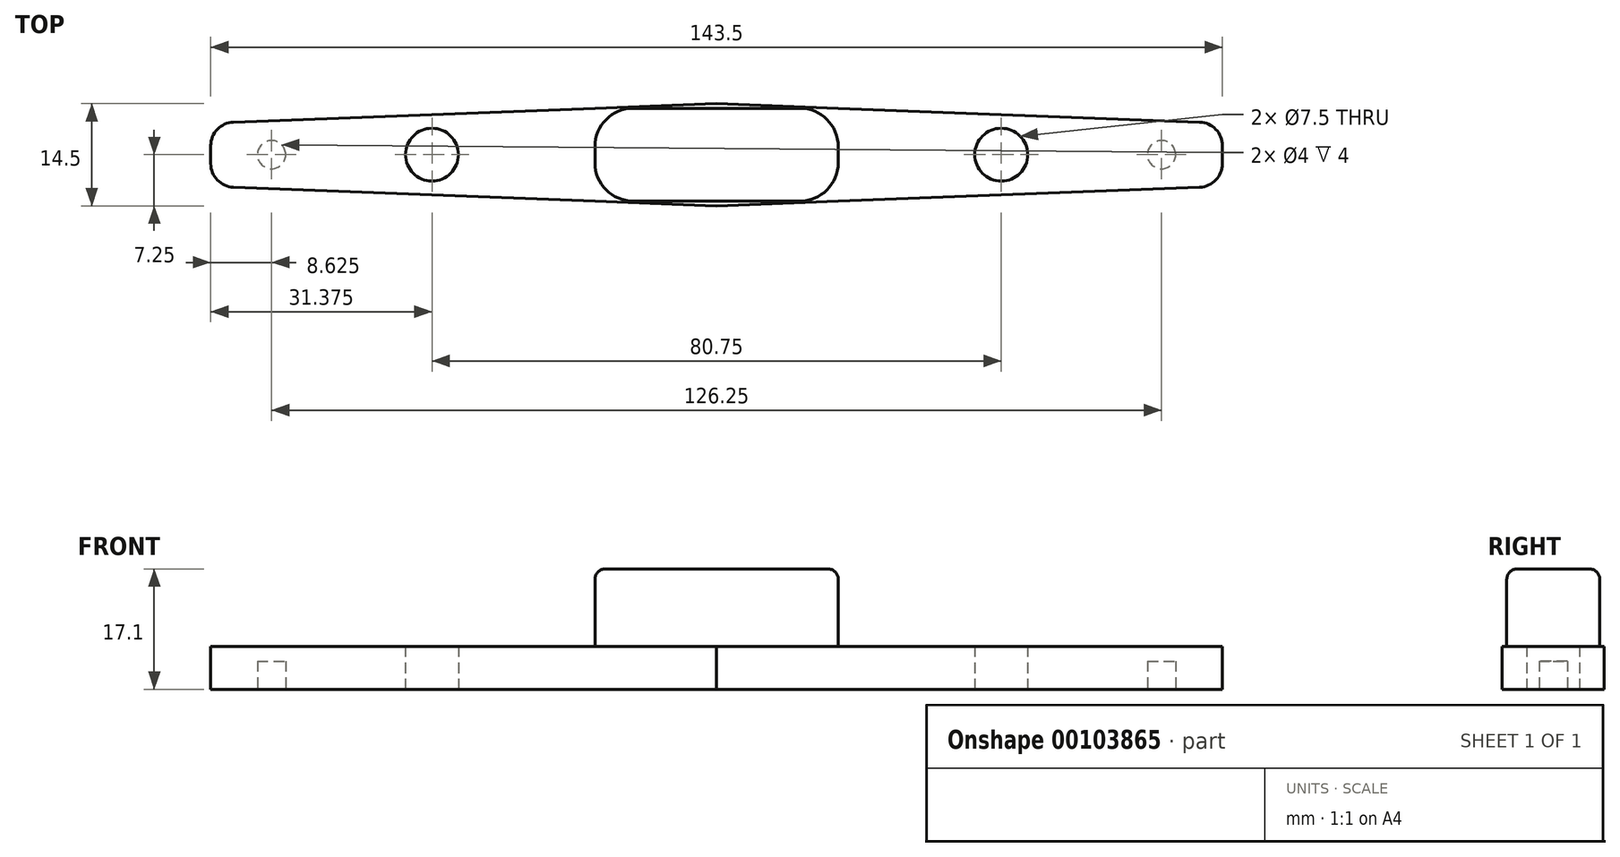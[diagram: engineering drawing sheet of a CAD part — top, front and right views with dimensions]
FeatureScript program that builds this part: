
annotation { "Feature Type Name" : "Feature", "Feature Type Description" : "" }
export const myFeature = defineFeature(function(context is Context, id is Id, definition is map)
    precondition{}
    {
        {
            var Q0;
            Q0=qCreatedBy(makeId("Top.planeOp"),FACE);
            var sketch = newSketch(context, id + "F0", { "sketchPlane" : qUnion([Q0])});
            skLineSegment(sketch, "E0", {"start": v(0, 7.25) * mm, "end": v(-71.75, 4.5) * mm});
            skLineSegment(sketch, "E1", {"start": v(-71.75, 4.5) * mm, "end": v(-71.75, -4.5) * mm});
            skLineSegment(sketch, "E2", {"start": v(-71.75, -4.5) * mm, "end": v(0, -7.25) * mm});
            skLineSegment(sketch, "E3", {"start": v(0, -7.25) * mm, "end": v(71.75, -4.5) * mm});
            skLineSegment(sketch, "E4", {"start": v(71.75, -4.5) * mm, "end": v(71.75, 4.5) * mm});
            skLineSegment(sketch, "E5", {"start": v(71.75, 4.5) * mm, "end": v(0, 7.25) * mm});
            skCircle(sketch, "E6", {"center": v(-40.37, 0) * mm, "radius": 3.75 * mm});
            skCircle(sketch, "E7", {"center": v(40.38, 0) * mm, "radius": 3.75 * mm});
            skSolve(sketch);
        }
        {
            var Q0;
            Q0=makeQuery(id+"F0.imprint","IMPRINT",FACE,{"disambiguationData":[TD([[makeQuery(id+"F0.imprint","IMPRINT",EDGE,{"derivedFrom":sQuery(id+"F0.wireOp",EDGE,"E0")}),1.0]])]});
            extrude(context, id + "F1", {"entities" : qUnion([Q0]), "depth" : 6.1 * mm});
        }
        {
            var Q0;
            Q0=makeQuery(id+"F1.opExtrude","CAP_FACE",FACE,{"disambiguationData":[OSD([sQuery(id+"F0.wireOp",EDGE,"E0"),sQuery(id+"F0.wireOp",EDGE,"E1"),sQuery(id+"F0.wireOp",EDGE,"E2"),sQuery(id+"F0.wireOp",EDGE,"E3"),sQuery(id+"F0.wireOp",EDGE,"E4"),sQuery(id+"F0.wireOp",EDGE,"E5"),sQuery(id+"F0.wireOp",EDGE,"E6"),sQuery(id+"F0.wireOp",EDGE,"E7")])],"isStart":false});
            var sketch = newSketch(context, id + "F2", { "sketchPlane" : qUnion([Q0])});
            skLineSegment(sketch, "E8.bottom", {"start": v(17.25, -6.59) * mm, "end": v(-17.25, -6.59) * mm});
            skLineSegment(sketch, "E8.top", {"start": v(17.25, 6.59) * mm, "end": v(-17.25, 6.59) * mm});
            skLineSegment(sketch, "E8.left", {"start": v(17.25, -6.59) * mm, "end": v(17.25, 6.59) * mm});
            skLineSegment(sketch, "E8.right", {"start": v(-17.25, -6.59) * mm, "end": v(-17.25, 6.59) * mm});
            skPoint(sketch, "E8.middle", {"position": v(0, 0) * mm});
            skSolve(sketch);
        }
        {
            var Q0;
            Q0 = qSketchRegion(id + "F2", true);
            extrude(context, id + "F3", {"entities" : qUnion([Q0]), "operationType" : NewBodyOperationType.ADD, "depth" : 11 * mm});
        }
        {
            var Q0;
            Q0=makeQuery(id+"F3.opExtrude","SWEPT_EDGE",EDGE,{"disambiguationData":[OSD([sQuery(id+"F0.wireOp",EDGE,"E2"),sQuery(id+"F2.wireOp",EDGE,"E8.bottom"),sQuery(id+"F2.wireOp",EDGE,"E8.right")])]});
            var Q1;
            Q1=makeQuery(id+"F3.opExtrude","SWEPT_EDGE",EDGE,{"disambiguationData":[OSD([sQuery(id+"F0.wireOp",EDGE,"E0"),sQuery(id+"F2.wireOp",EDGE,"E8.top"),sQuery(id+"F2.wireOp",EDGE,"E8.right")])]});
            var Q2;
            Q2=makeQuery(id+"F3.opExtrude","SWEPT_EDGE",EDGE,{"disambiguationData":[OSD([sQuery(id+"F0.wireOp",EDGE,"E3"),sQuery(id+"F2.wireOp",EDGE,"E8.bottom"),sQuery(id+"F2.wireOp",EDGE,"E8.left")])]});
            var Q3;
            Q3=makeQuery(id+"F3.opExtrude","SWEPT_EDGE",EDGE,{"disambiguationData":[OSD([sQuery(id+"F0.wireOp",EDGE,"E5"),sQuery(id+"F2.wireOp",EDGE,"E8.top"),sQuery(id+"F2.wireOp",EDGE,"E8.left")])]});
            fillet(context, id + "F4", {"entities" : qUnion([Q0, Q1, Q2, Q3]), "radius" : 5.44 * mm, "tangentPropagation" : true, "allowEdgeOverflow" : false});
        }
        {
            var Q0;
            Q0=makeQuery(id+"F3.opExtrude","CAP_EDGE",EDGE,{"disambiguationData":[OSD([sQuery(id+"F2.wireOp",EDGE,"E8.top")])],"isStart":false});
            var Q1;
            {var subQ0=sQuery(id+"F2.wireOp",EDGE,"E8.left");var subQ1=sQuery(id+"F2.wireOp",EDGE,"E8.top");Q1=makeQuery(id+"F4.opFillet","BLEND_EDGE",EDGE,{"blendedFrom":[makeQuery(id+"F3.opExtrude","SWEPT_EDGE",EDGE,{"disambiguationData":[OSD([sQuery(id+"F0.wireOp",EDGE,"E5"),subQ1,subQ0])]}),makeQuery(id+"F3.opExtrude","CAP_FACE",FACE,{"disambiguationData":[OSD([sQuery(id+"F2.wireOp",EDGE,"E8.bottom"),subQ1,subQ0,sQuery(id+"F2.wireOp",EDGE,"E8.right")])],"isStart":false})],"blendedInto":[makeQuery(id+"F3.opExtrude","CAP_FACE",FACE,{"disambiguationData":[OSD([sQuery(id+"F2.wireOp",EDGE,"E8.bottom"),subQ1,subQ0,sQuery(id+"F2.wireOp",EDGE,"E8.right")])],"isStart":false})]});}
            var Q2;
            Q2=makeQuery(id+"F3.opExtrude","CAP_EDGE",EDGE,{"disambiguationData":[OSD([sQuery(id+"F2.wireOp",EDGE,"E8.left")])],"isStart":false});
            var Q3;
            {var subQ0=sQuery(id+"F2.wireOp",EDGE,"E8.left");var subQ1=sQuery(id+"F2.wireOp",EDGE,"E8.bottom");Q3=makeQuery(id+"F4.opFillet","BLEND_EDGE",EDGE,{"blendedFrom":[makeQuery(id+"F3.opExtrude","SWEPT_EDGE",EDGE,{"disambiguationData":[OSD([sQuery(id+"F0.wireOp",EDGE,"E3"),subQ1,subQ0])]}),makeQuery(id+"F3.opExtrude","CAP_FACE",FACE,{"disambiguationData":[OSD([subQ1,sQuery(id+"F2.wireOp",EDGE,"E8.top"),subQ0,sQuery(id+"F2.wireOp",EDGE,"E8.right")])],"isStart":false})],"blendedInto":[makeQuery(id+"F3.opExtrude","CAP_FACE",FACE,{"disambiguationData":[OSD([subQ1,sQuery(id+"F2.wireOp",EDGE,"E8.top"),subQ0,sQuery(id+"F2.wireOp",EDGE,"E8.right")])],"isStart":false})]});}
            var Q4;
            Q4=makeQuery(id+"F3.opExtrude","CAP_EDGE",EDGE,{"disambiguationData":[OSD([sQuery(id+"F2.wireOp",EDGE,"E8.bottom")])],"isStart":false});
            var Q5;
            {var subQ0=sQuery(id+"F2.wireOp",EDGE,"E8.right");var subQ1=sQuery(id+"F2.wireOp",EDGE,"E8.bottom");Q5=makeQuery(id+"F4.opFillet","BLEND_EDGE",EDGE,{"blendedFrom":[makeQuery(id+"F3.opExtrude","SWEPT_EDGE",EDGE,{"disambiguationData":[OSD([sQuery(id+"F0.wireOp",EDGE,"E2"),subQ1,subQ0])]}),makeQuery(id+"F3.opExtrude","CAP_FACE",FACE,{"disambiguationData":[OSD([subQ1,sQuery(id+"F2.wireOp",EDGE,"E8.top"),sQuery(id+"F2.wireOp",EDGE,"E8.left"),subQ0])],"isStart":false})],"blendedInto":[makeQuery(id+"F3.opExtrude","CAP_FACE",FACE,{"disambiguationData":[OSD([subQ1,sQuery(id+"F2.wireOp",EDGE,"E8.top"),sQuery(id+"F2.wireOp",EDGE,"E8.left"),subQ0])],"isStart":false})]});}
            var Q6;
            Q6=makeQuery(id+"F3.opExtrude","CAP_EDGE",EDGE,{"disambiguationData":[OSD([sQuery(id+"F2.wireOp",EDGE,"E8.right")])],"isStart":false});
            var Q7;
            {var subQ0=sQuery(id+"F2.wireOp",EDGE,"E8.right");var subQ1=sQuery(id+"F2.wireOp",EDGE,"E8.top");Q7=makeQuery(id+"F4.opFillet","BLEND_EDGE",EDGE,{"blendedFrom":[makeQuery(id+"F3.opExtrude","SWEPT_EDGE",EDGE,{"disambiguationData":[OSD([sQuery(id+"F0.wireOp",EDGE,"E0"),subQ1,subQ0])]}),makeQuery(id+"F3.opExtrude","CAP_FACE",FACE,{"disambiguationData":[OSD([sQuery(id+"F2.wireOp",EDGE,"E8.bottom"),subQ1,sQuery(id+"F2.wireOp",EDGE,"E8.left"),subQ0])],"isStart":false})],"blendedInto":[makeQuery(id+"F3.opExtrude","CAP_FACE",FACE,{"disambiguationData":[OSD([sQuery(id+"F2.wireOp",EDGE,"E8.bottom"),subQ1,sQuery(id+"F2.wireOp",EDGE,"E8.left"),subQ0])],"isStart":false})]});}
            fillet(context, id + "F5", {"entities" : qUnion([Q0, Q1, Q2, Q3, Q4, Q5, Q6, Q7]), "radius" : 1.5 * mm, "tangentPropagation" : true, "allowEdgeOverflow" : false});
        }
        {
            var Q0;
            Q0=makeQuery(id+"F1.opExtrude","CAP_FACE",FACE,{"disambiguationData":[OSD([sQuery(id+"F0.wireOp",EDGE,"E0"),sQuery(id+"F0.wireOp",EDGE,"E1"),sQuery(id+"F0.wireOp",EDGE,"E2"),sQuery(id+"F0.wireOp",EDGE,"E3"),sQuery(id+"F0.wireOp",EDGE,"E4"),sQuery(id+"F0.wireOp",EDGE,"E5"),sQuery(id+"F0.wireOp",EDGE,"E6"),sQuery(id+"F0.wireOp",EDGE,"E7")])],"isStart":true});
            var sketch = newSketch(context, id + "F6", { "sketchPlane" : qUnion([Q0])});
            skCircle(sketch, "E9", {"center": v(-63.12, 0) * mm, "radius": 2 * mm});
            skCircle(sketch, "E10", {"center": v(63.13, 0) * mm, "radius": 2 * mm});
            skSolve(sketch);
        }
        {
            var Q0;
            Q0=makeQuery(id+"F6.imprint","IMPRINT",FACE,{"disambiguationData":[TD([[makeQuery(id+"F6.imprint","IMPRINT",EDGE,{"derivedFrom":sQuery(id+"F6.wireOp",EDGE,"E9")}),1.0]])]});
            var Q1;
            Q1=makeQuery(id+"F6.imprint","IMPRINT",FACE,{"disambiguationData":[TD([[makeQuery(id+"F6.imprint","IMPRINT",EDGE,{"derivedFrom":sQuery(id+"F6.wireOp",EDGE,"E10")}),1.0]])]});
            extrude(context, id + "F7", {"entities" : qUnion([Q0, Q1]), "operationType" : NewBodyOperationType.REMOVE, "oppositeDirection" : true, "depth" : 4 * mm});
        }
        {
            var Q0;
            Q0=makeQuery(id+"F1.opExtrude","SWEPT_EDGE",EDGE,{"disambiguationData":[OSD([sQuery(id+"F0.wireOp",EDGE,"E4"),sQuery(id+"F0.wireOp",EDGE,"E5")])]});
            var Q1;
            Q1=makeQuery(id+"F1.opExtrude","SWEPT_EDGE",EDGE,{"disambiguationData":[OSD([sQuery(id+"F0.wireOp",EDGE,"E3"),sQuery(id+"F0.wireOp",EDGE,"E4")])]});
            var Q2;
            Q2=makeQuery(id+"F1.opExtrude","SWEPT_EDGE",EDGE,{"disambiguationData":[OSD([sQuery(id+"F0.wireOp",EDGE,"E0"),sQuery(id+"F0.wireOp",EDGE,"E1")])]});
            var Q3;
            Q3=makeQuery(id+"F1.opExtrude","SWEPT_EDGE",EDGE,{"disambiguationData":[OSD([sQuery(id+"F0.wireOp",EDGE,"E1"),sQuery(id+"F0.wireOp",EDGE,"E2")])]});
            fillet(context, id + "F8", {"entities" : qUnion([Q0, Q1, Q2, Q3]), "radius" : 3.36 * mm, "tangentPropagation" : true, "allowEdgeOverflow" : false});
        }
    });
